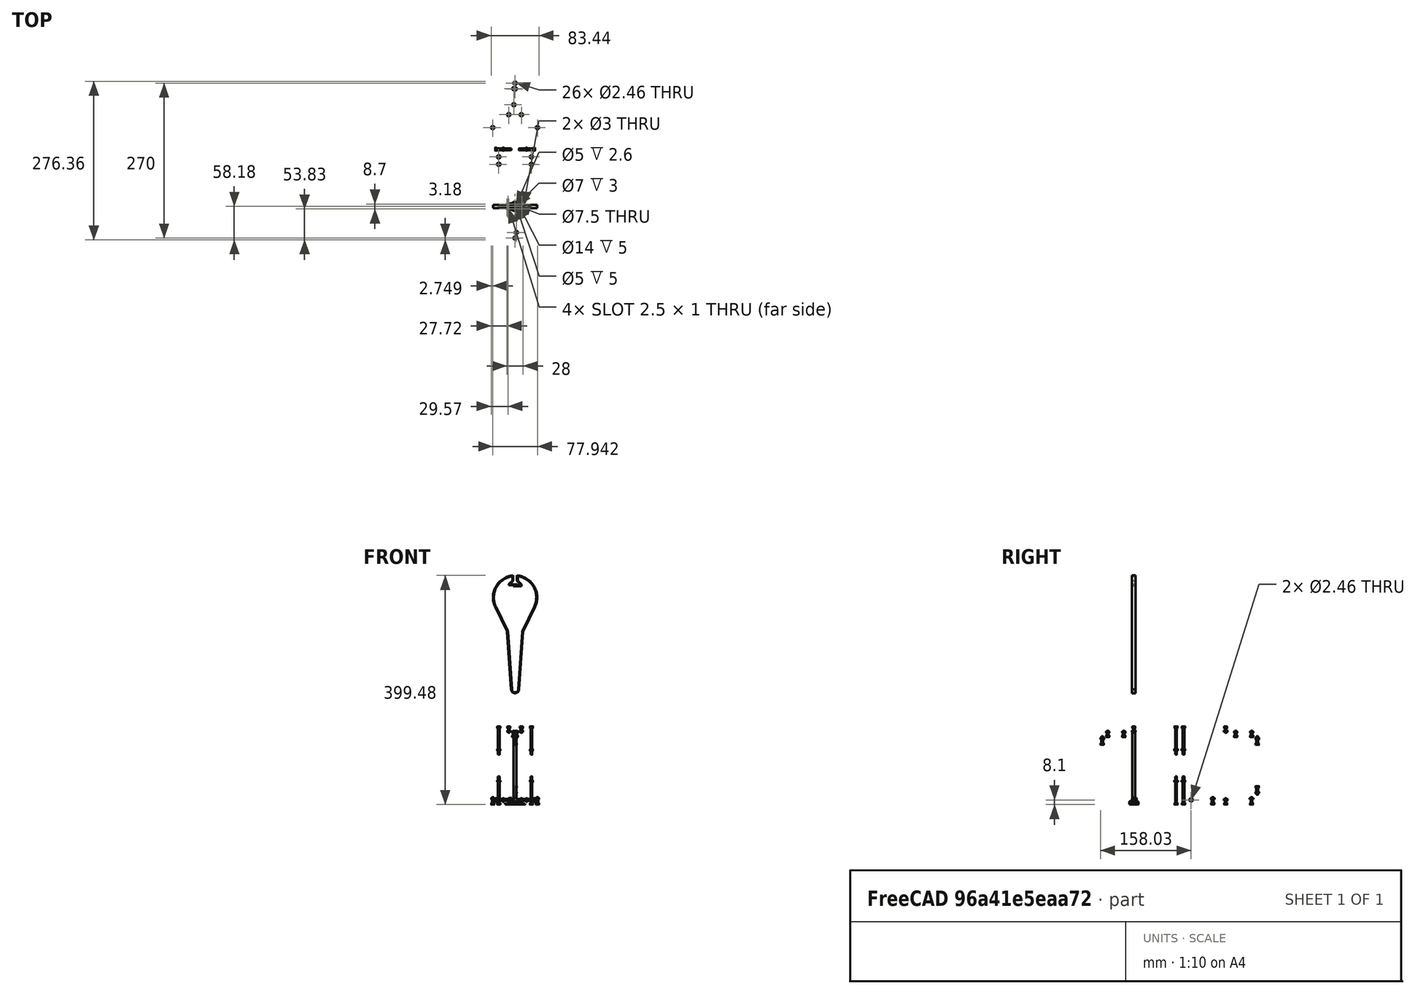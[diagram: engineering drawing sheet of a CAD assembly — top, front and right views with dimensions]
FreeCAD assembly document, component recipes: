
FREECAD ASSEMBLY — COMPONENT RECIPES ("AssemblyArt2")

This assembly document has 7 components, labeled P0..P6 below (a component is one placed body or linked part). 0 of them carry a construction recipe — the FreeCAD feature program that regenerates the part from scratch, quoted from this document or its linked companion documents; the rest are supplied as boundary geometry only. No exploded tour is included for this assembly.
COMPONENT P0 — geometry summary ("Bearing_625ZZ"; no construction recipe available for this part):
  bounding box: 16.0 x 16.0 x 5.0 mm
  tessellated surface: 4,648 triangles
  volume: 876 mm^3 (68% of its bounding box)
  symmetry: 2-fold rotationally symmetric about the x axis; 2-fold rotationally symmetric about the y axis; revolution-symmetric about the z axis through its bounding-box center; mirror-symmetric across its x mid-plane, y mid-plane
COMPONENT P1 — geometry summary ("Bearing_MF84ZZ"; no construction recipe available for this part):
  bounding box: 9.2 x 9.2 x 3.0 mm
  tessellated surface: 4,220 triangles
  volume: 122 mm^3 (48% of its bounding box)
  symmetry: revolution-symmetric about the z axis through its bounding-box center; mirror-symmetric across its y mid-plane
COMPONENT P2 — geometry summary ("GT2_Belt_Art3"; no construction recipe available for this part):
  bounding box: 205.4 x 77.0 x 6.0 mm
  tessellated surface: 1,344 triangles
  volume: 4691 mm^3 (5% of its bounding box)
  symmetry: mirror-symmetric across its y mid-plane
COMPONENT P3 — geometry summary ("Magnet"; no construction recipe available for this part):
  bounding box: 8.0 x 8.0 x 1.0 mm
  tessellated surface: 500 triangles
  volume: 50 mm^3 (79% of its bounding box)
  symmetry: 2-fold rotationally symmetric about the y axis; revolution-symmetric about the z axis through its bounding-box center; mirror-symmetric across its y mid-plane, z mid-plane
COMPONENT P4 — geometry summary ("OpticSensor"; no construction recipe available for this part):
  bounding box: 35.0 x 11.5 x 11.0 mm
  tessellated surface: 1,436 triangles
  volume: 1323 mm^3 (30% of its bounding box)
COMPONENT P5 — geometry summary ("5x128mm"; no construction recipe available for this part):
  bounding box: 128.0 x 5.0 x 5.0 mm
  tessellated surface: 360 triangles
  volume: 2513 mm^3 (79% of its bounding box)
  symmetry: 2-fold rotationally symmetric about the x axis; 2-fold rotationally symmetric about the y axis; revolution-symmetric about the z axis through its bounding-box center; mirror-symmetric across its x mid-plane, y mid-plane, z mid-plane
COMPONENT P6 — geometry summary ("4x14mm"; no construction recipe available for this part):
  bounding box: 14.0 x 4.0 x 4.0 mm
  tessellated surface: 288 triangles
  volume: 176 mm^3 (79% of its bounding box)
  symmetry: 2-fold rotationally symmetric about the x axis; 6-fold rotationally symmetric about the z axis; mirror-symmetric across its x mid-plane, y mid-plane, z mid-plane
PROVENANCE & LICENSES
A FreeCAD (.FCStd) document from a public repository crawl; recipes are the document's own serialized feature recipes (and, for linked parts, companion documents' recipes).
License: as declared in the source repository (recorded in the dataset sidecar).
